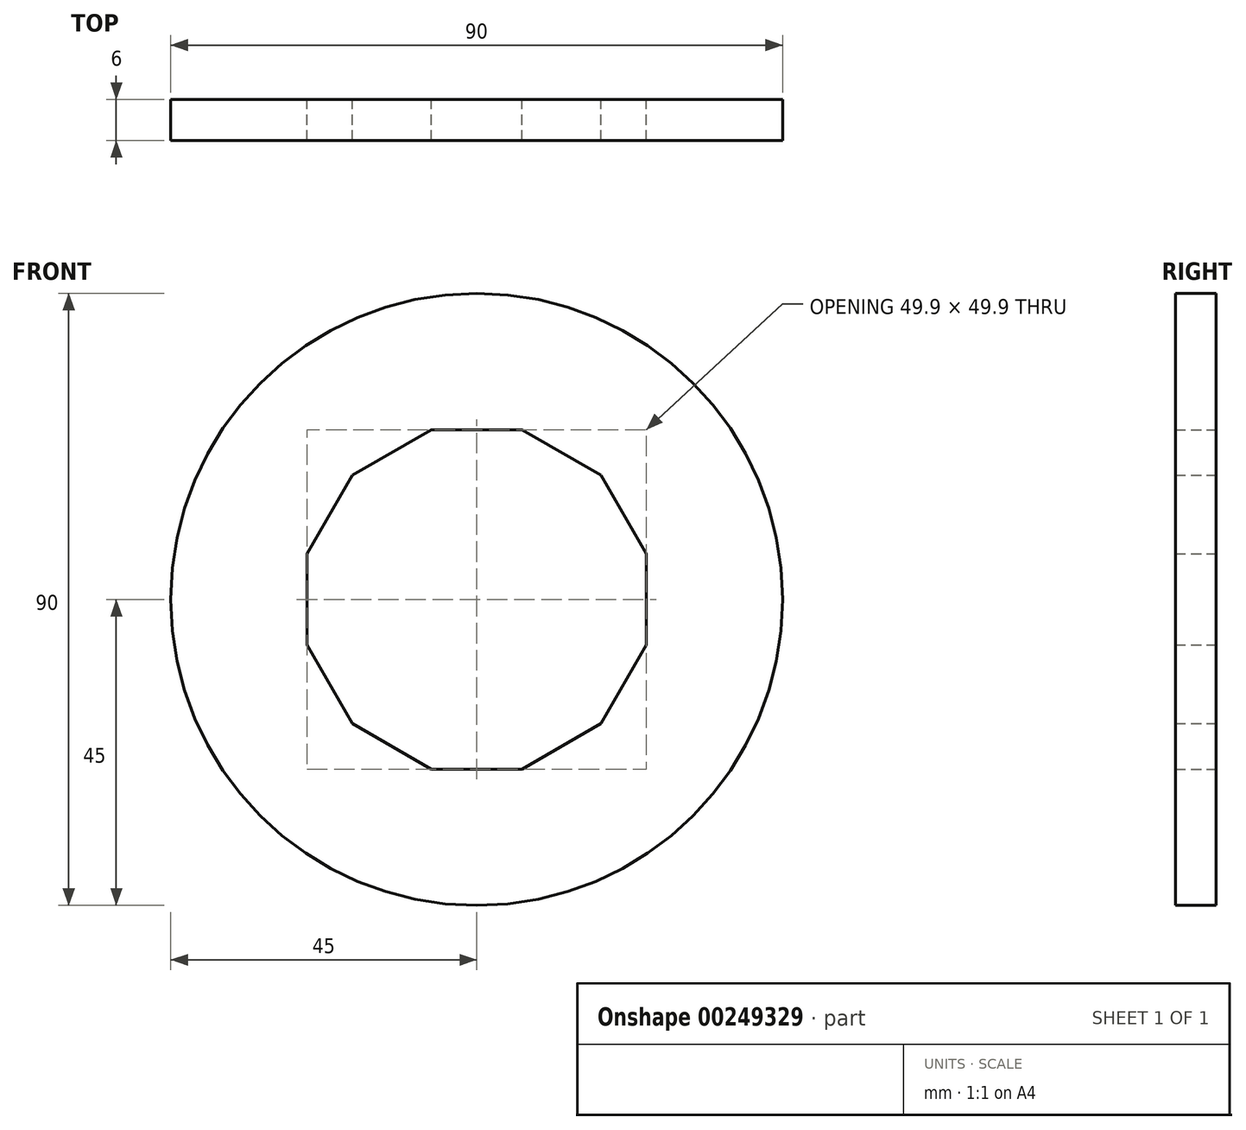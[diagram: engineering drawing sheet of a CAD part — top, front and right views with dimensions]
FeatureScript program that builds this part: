
annotation { "Feature Type Name" : "Feature", "Feature Type Description" : "" }
export const myFeature = defineFeature(function(context is Context, id is Id, definition is map)
    precondition{}
    {
        {
            var Q0;
            Q0=qCreatedBy(makeId("Front.planeOp"),FACE);
            var sketch = newSketch(context, id + "F0", { "sketchPlane" : qUnion([Q0])});
            skCircle(sketch, "E0.cCircle", {"center": v(0, 0) * mm, "radius": 24.95 * mm, "construction": true});
            skLineSegment(sketch, "E0.0", {"start": v(-6.69, 24.95) * mm, "end": v(6.69, 24.95) * mm});
            skLineSegment(sketch, "E0.1", {"start": v(6.69, 24.95) * mm, "end": v(18.26, 18.26) * mm});
            skLineSegment(sketch, "E0.2", {"start": v(18.26, 18.26) * mm, "end": v(24.95, 6.69) * mm});
            skLineSegment(sketch, "E0.3", {"start": v(24.95, 6.69) * mm, "end": v(24.95, -6.69) * mm});
            skLineSegment(sketch, "E0.4", {"start": v(24.95, -6.69) * mm, "end": v(18.26, -18.26) * mm});
            skLineSegment(sketch, "E0.5", {"start": v(18.26, -18.26) * mm, "end": v(6.69, -24.95) * mm});
            skLineSegment(sketch, "E0.6", {"start": v(6.69, -24.95) * mm, "end": v(-6.69, -24.95) * mm});
            skLineSegment(sketch, "E0.7", {"start": v(-6.69, -24.95) * mm, "end": v(-18.26, -18.26) * mm});
            skLineSegment(sketch, "E0.8", {"start": v(-18.26, -18.26) * mm, "end": v(-24.95, -6.69) * mm});
            skLineSegment(sketch, "E0.9", {"start": v(-24.95, -6.69) * mm, "end": v(-24.95, 6.69) * mm});
            skLineSegment(sketch, "E0.10", {"start": v(-24.95, 6.69) * mm, "end": v(-18.26, 18.26) * mm});
            skLineSegment(sketch, "E0.11", {"start": v(-18.26, 18.26) * mm, "end": v(-6.69, 24.95) * mm});
            skPoint(sketch, "E0.0.midPoint", {"position": v(0, 24.95) * mm});
            skCircle(sketch, "E1", {"center": v(0, 0) * mm, "radius": 45 * mm});
            skSolve(sketch);
        }
        {
            var Q0;
            Q0=makeQuery(id+"F0.imprint","IMPRINT",FACE,{"disambiguationData":[TD([[makeQuery(id+"F0.imprint","IMPRINT",EDGE,{"derivedFrom":sQuery(id+"F0.wireOp",EDGE,"E0.0")}),1.0]])]});
            extrude(context, id + "F1", {"entities" : qUnion([Q0]), "depth" : 6 * mm});
        }
    });
